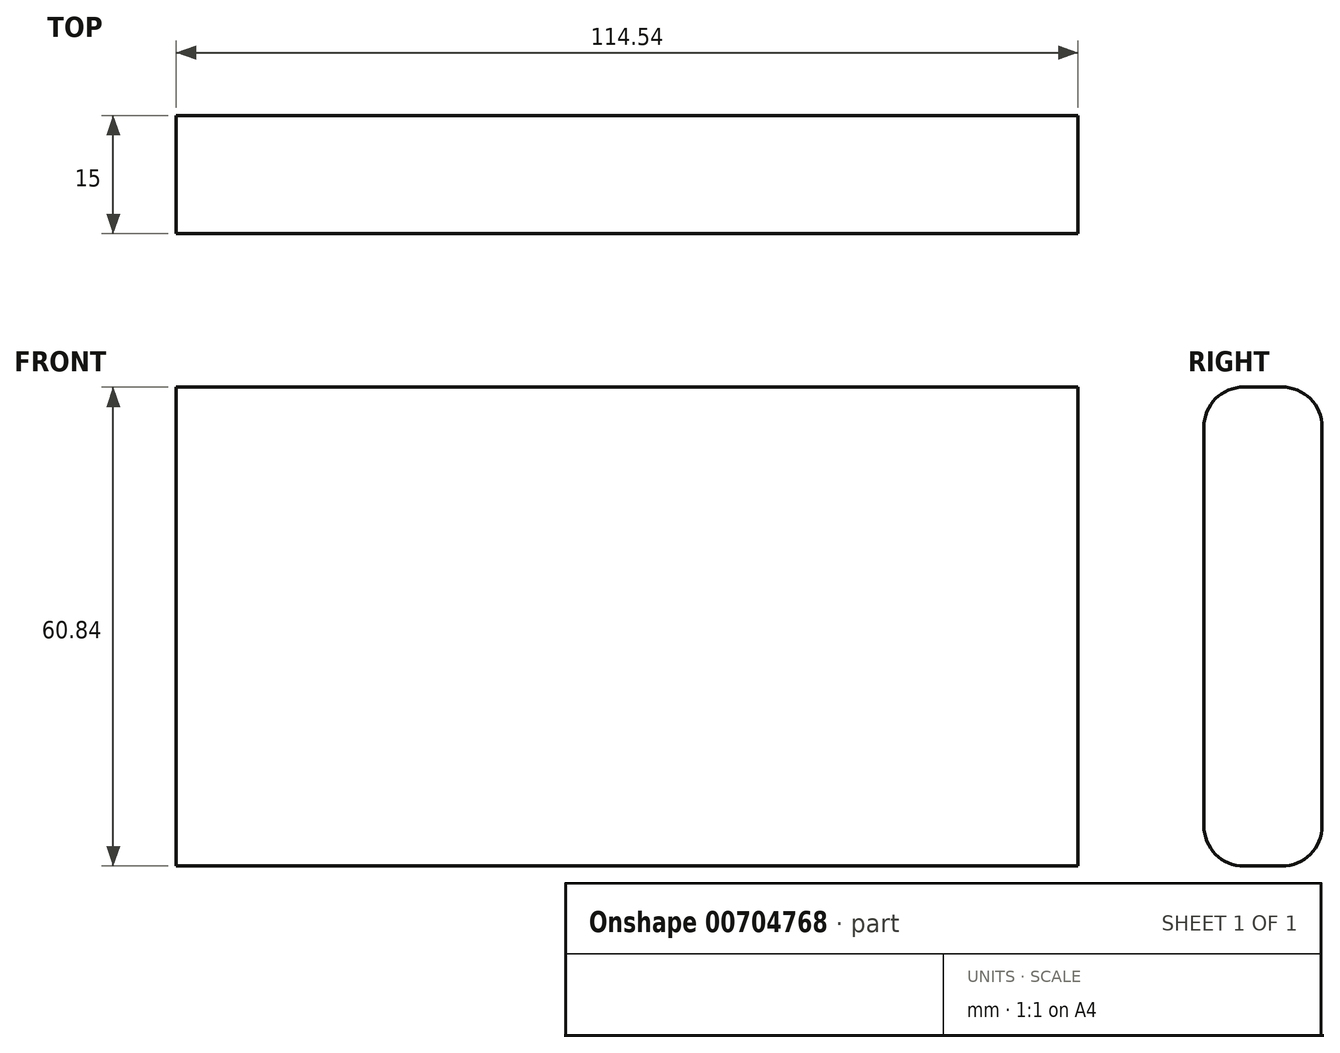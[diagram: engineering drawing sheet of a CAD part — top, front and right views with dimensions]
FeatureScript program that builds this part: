
annotation { "Feature Type Name" : "Feature", "Feature Type Description" : "" }
export const myFeature = defineFeature(function(context is Context, id is Id, definition is map)
    precondition{}
    {
        {
            var Q0;
            Q0=qCreatedBy(makeId("Front.planeOp"),FACE);
            var sketch = newSketch(context, id + "F0", { "sketchPlane" : qUnion([Q0])});
            skLineSegment(sketch, "E0.bottom", {"start": v(57.27, -30.42) * mm, "end": v(-57.27, -30.42) * mm});
            skLineSegment(sketch, "E0.top", {"start": v(57.27, 30.42) * mm, "end": v(-57.27, 30.42) * mm});
            skLineSegment(sketch, "E0.left", {"start": v(57.27, -30.42) * mm, "end": v(57.27, 30.42) * mm});
            skLineSegment(sketch, "E0.right", {"start": v(-57.27, -30.42) * mm, "end": v(-57.27, 30.42) * mm});
            skPoint(sketch, "E0.middle", {"position": v(0, 0) * mm});
            skSolve(sketch);
        }
        {
            var Q0;
            Q0 = qSketchRegion(id + "F0", true);
            var sketch = newSketch(context, id + "F1", { "sketchPlane" : qUnion([Q0])});
            skSolve(sketch);
        }
        {
            var Q0;
            Q0=makeQuery(id+"F1.imprint","IMPRINT",FACE,{"disambiguationData":[TD([[makeQuery(id+"F1.imprint","IMPRINT",EDGE,{"derivedFrom":makeQuery(id+"F0.imprint","IMPRINT",EDGE,{"derivedFrom":sQuery(id+"F0.wireOp",EDGE,"E0.bottom")})}),-1.0]])]});
            extrude(context, id + "F2", {"entities" : qUnion([Q0]), "depth" : 15 * mm, "offsetDistance" : 25.4 * mm});
        }
        {
            var Q0;
            Q0=makeQuery(id+"F2.opExtrude","CAP_EDGE",EDGE,{"disambiguationData":[OSD([sQuery(id+"F0.wireOp",EDGE,"E0.bottom")])],"isStart":false});
            var Q1;
            Q1=makeQuery(id+"F2.opExtrude","CAP_EDGE",EDGE,{"disambiguationData":[OSD([sQuery(id+"F0.wireOp",EDGE,"E0.top")])],"isStart":false});
            var Q2;
            Q2=makeQuery(id+"F2.opExtrude","CAP_EDGE",EDGE,{"disambiguationData":[OSD([sQuery(id+"F0.wireOp",EDGE,"E0.bottom")])],"isStart":true});
            var Q3;
            Q3=makeQuery(id+"F2.opExtrude","CAP_EDGE",EDGE,{"disambiguationData":[OSD([sQuery(id+"F0.wireOp",EDGE,"E0.top")])],"isStart":true});
            fillet(context, id + "F3", {"entities" : qUnion([Q0, Q1, Q2, Q3]), "radius" : 5.08 * mm, "tangentPropagation" : true, "allowEdgeOverflow" : false});
        }
    });
